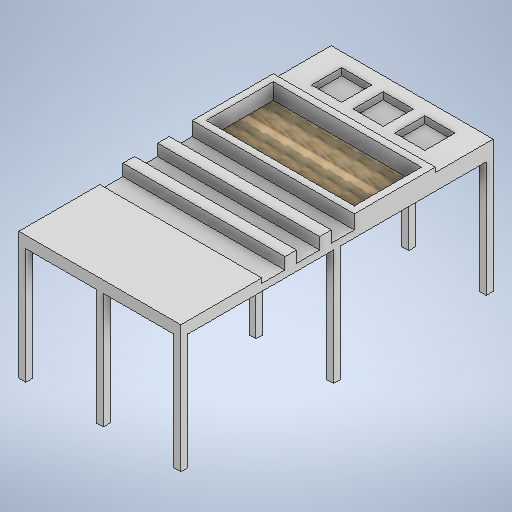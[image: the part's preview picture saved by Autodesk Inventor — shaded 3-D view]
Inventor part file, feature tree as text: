
AUTODESK INVENTOR PART (.ipt)
format: ipt  version: 2025 (Build 290162000, 162)  size: 399,872 bytes
history: native  units: in
note: dims shown in document units (in); Inventor stores cm internally (conversion verified against a paired STEP export)
features: extrude x8, sketch x4
ambient origin geometry x8: Origin, YZ Plane, XZ Plane, XY Plane, X Axis, Y Axis, Z Axis, Center Point
bodies: Solid1 (feature_tree)
feature tree (12):
  sketch  "Sketch1"  dims[d1=53.1496in d2=27.5591in]
  extrude  "Extrusion1"  Depth=27.5591in
  extrude  "Extrusion2"  Depth=15.748in
  extrude  "Extrusion3"  Depth=1.9685in TaperAngle=0.0deg
  extrude  "Extrusion4"  Depth=3.5433in TaperAngle=0.0deg
  sketch  "Sketch2"  dims[d3=13.7795in d4=15.748in]
  extrude  "Extrusion5"  Depth=2.7559in TaperAngle=0.0deg
  extrude  "Extrusion6"  Depth=1.1811in
  extrude  "Extrusion8"  Depth=1.1811in
  extrude  "Extrusion9"  Depth=1.1811in
  sketch  "Sketch4"  dims[d5=13.7795in d6=1.9685in d7=0.0in]
  sketch  "Sketch5"  dims[d8=1.1811in d9=0.0in d10=3.5433in d11=0.0in d12=2.7559in d13=0.0in d14=1.1811in d15=1.1811in d16=1.1811in d17=1.1811in d18=5.1181in d19=5.1181in d20=4.1339in d21=2.3622in d22=1.9685in d23=1.9685in d24=2.7559in d25=0.0in d26=1.9685in d27=0.0in d32=1.1811in d33=1.1811in d34=19.685in d35=0.0in d36=27.5591in d37=1.9685in d38=1.9685in d39=3.937in d40=3.937in d41=1.9685in d42=0.0in]
